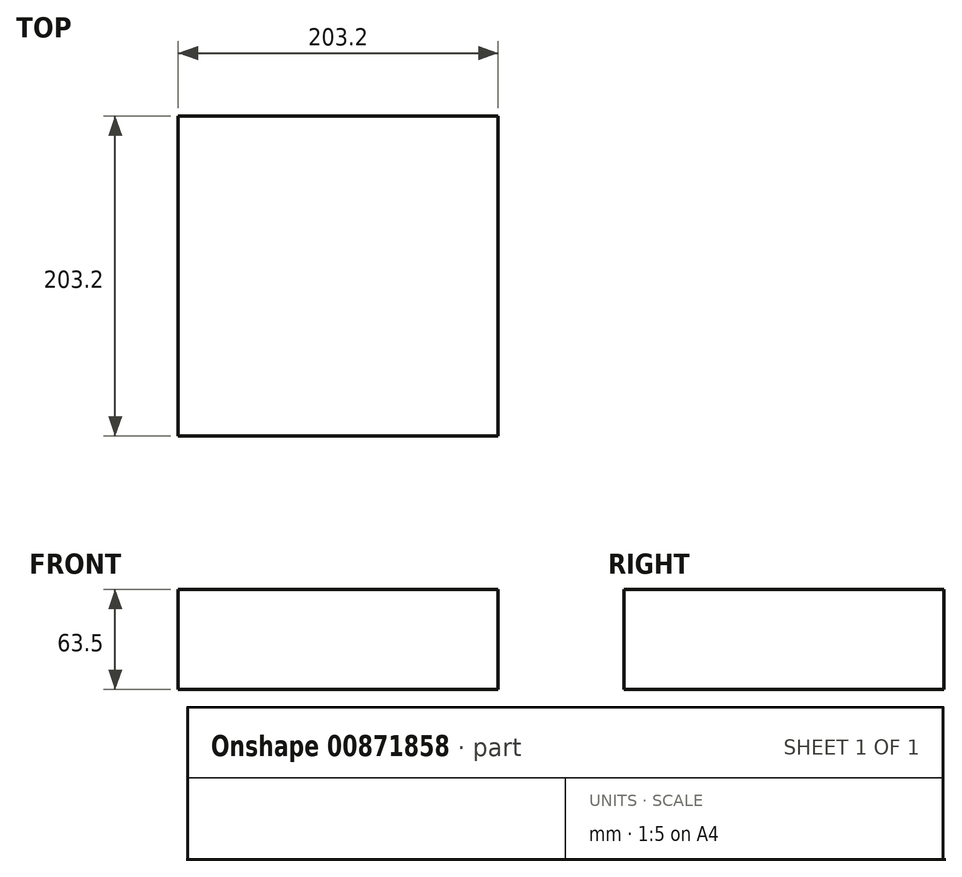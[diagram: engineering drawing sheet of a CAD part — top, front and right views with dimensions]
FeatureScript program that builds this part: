
annotation { "Feature Type Name" : "Feature", "Feature Type Description" : "" }
export const myFeature = defineFeature(function(context is Context, id is Id, definition is map)
    precondition{}
    {
        {
            var Q0;
            Q0=qCreatedBy(makeId("Top.planeOp"),FACE);
            var sketch = newSketch(context, id + "F0", { "sketchPlane" : qUnion([Q0])});
            skLineSegment(sketch, "E0.bottom", {"start": v(-178.28, 180.4) * mm, "end": v(24.92, 180.4) * mm});
            skLineSegment(sketch, "E0.top", {"start": v(-178.28, -22.8) * mm, "end": v(24.92, -22.8) * mm});
            skLineSegment(sketch, "E0.left", {"start": v(-178.28, 180.4) * mm, "end": v(-178.28, -22.8) * mm});
            skLineSegment(sketch, "E0.right", {"start": v(24.92, 180.4) * mm, "end": v(24.92, -22.8) * mm});
            skSolve(sketch);
        }
        {
            var Q0;
            Q0=makeQuery(id+"F0.imprint","IMPRINT",FACE,{"disambiguationData":[TD([[makeQuery(id+"F0.imprint","IMPRINT",EDGE,{"derivedFrom":sQuery(id+"F0.wireOp",EDGE,"E0.bottom")}),-1.0]])]});
            extrude(context, id + "F1", {"entities" : qUnion([Q0]), "depth" : 63.5 * mm, "offsetDistance" : 25.4 * mm});
        }
    });
